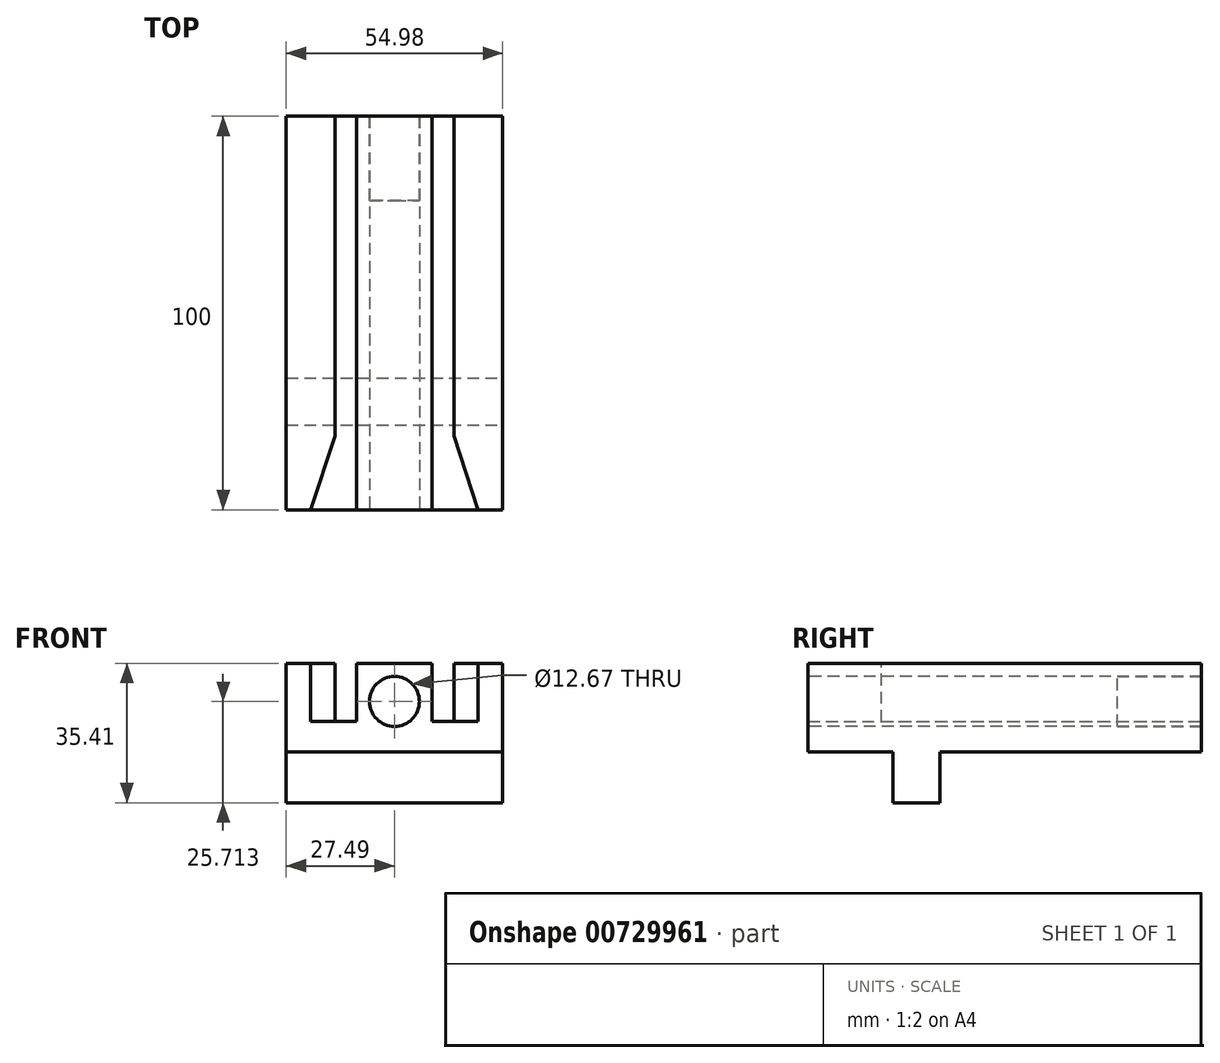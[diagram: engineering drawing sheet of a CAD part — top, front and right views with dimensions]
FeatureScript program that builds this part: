
annotation { "Feature Type Name" : "Feature", "Feature Type Description" : "" }
export const myFeature = defineFeature(function(context is Context, id is Id, definition is map)
    precondition{}
    {
        {
            var Q0;
            Q0=qCreatedBy(makeId("Front.planeOp"),FACE);
            var sketch = newSketch(context, id + "F0", { "sketchPlane" : qUnion([Q0])});
            skLineSegment(sketch, "E0.bottom", {"start": v(15.1, 10.3) * mm, "end": v(9.57, 10.3) * mm});
            skLineSegment(sketch, "E0.top", {"start": v(27.49, -10.3) * mm, "end": v(-27.49, -10.3) * mm});
            skLineSegment(sketch, "E0.left", {"start": v(27.49, 10.3) * mm, "end": v(27.49, -10.3) * mm});
            skLineSegment(sketch, "E0.right", {"start": v(-27.49, 10.3) * mm, "end": v(-27.49, -10.3) * mm});
            skPoint(sketch, "E0.middle", {"position": v(0, 0) * mm});
            skLineSegment(sketch, "E1.top", {"start": v(-9.57, 25.12) * mm, "end": v(9.57, 25.12) * mm});
            skLineSegment(sketch, "E1.left", {"start": v(-9.57, 10.3) * mm, "end": v(-9.57, 25.12) * mm});
            skLineSegment(sketch, "E1.right", {"start": v(9.57, 10.3) * mm, "end": v(9.57, 25.12) * mm});
            skPoint(sketch, "E1.middle", {"position": v(0, 10.3) * mm});
            skLineSegment(sketch, "E2.bottom", {"start": v(-27.49, -10.3) * mm, "end": v(-15.1, -10.3) * mm});
            skLineSegment(sketch, "E2.left", {"start": v(-27.49, -10.3) * mm, "end": v(-27.49, 25.12) * mm});
            skLineSegment(sketch, "E2.right", {"start": v(-15.1, 10.3) * mm, "end": v(-15.1, 25.12) * mm});
            skPoint(sketch, "E2.middle", {"position": v(-21.3, 25.12) * mm});
            skLineSegment(sketch, "E3", {"start": v(-15.1, 25.12) * mm, "end": v(-27.49, 25.12) * mm});
            skPoint(sketch, "E4.orphan", {"position": v(-15.1, 60.53) * mm});
            skPoint(sketch, "E5.orphan", {"position": v(-27.49, 60.53) * mm});
            skPoint(sketch, "E1.bottom.end.orphan", {"position": v(9.57, -4.53) * mm});
            skPoint(sketch, "E1.bottom.start.orphan", {"position": v(-9.57, -4.53) * mm});
            skLineSegment(sketch, "E6.trimOffspring", {"start": v(-9.57, 10.3) * mm, "end": v(-15.1, 10.3) * mm});
            skLineSegment(sketch, "E7.MirrorCS", {"start": v(15.1, 10.3) * mm, "end": v(15.1, 25.12) * mm});
            skLineSegment(sketch, "E8.MirrorCS", {"start": v(15.1, 25.12) * mm, "end": v(27.49, 25.12) * mm});
            skLineSegment(sketch, "E9.MirrorCS", {"start": v(27.49, -10.3) * mm, "end": v(27.49, 25.12) * mm});
            skSolve(sketch);
        }
        {
            var Q0;
            Q0 = qSketchRegion(id + "F0", true);
            extrude(context, id + "F1", {"entities" : qUnion([Q0]), "endBound" : BoundingType.SYMMETRIC, "depth" : 100 * mm, "offsetDistance" : 25 * mm});
        }
        {
            var Q0;
            Q0=makeQuery(id+"F1.opExtrude","SWEPT_FACE",FACE,{"disambiguationData":[OSD([sQuery(id+"F0.wireOp",EDGE,"E0.top"),sQuery(id+"F0.wireOp",EDGE,"E2.bottom")])]});
            var sketch = newSketch(context, id + "F2", { "sketchPlane" : qUnion([Q0])});
            skLineSegment(sketch, "E10.0.0", {"start": v(-27.49, -50) * mm, "end": v(27.49, -50) * mm, "construction": true});
            skLineSegment(sketch, "E10.0.1", {"start": v(27.49, -50) * mm, "end": v(27.49, 50) * mm, "construction": true});
            skLineSegment(sketch, "E10.0.2", {"start": v(27.49, 50) * mm, "end": v(-27.49, 50) * mm, "construction": true});
            skLineSegment(sketch, "E10.0.3", {"start": v(-27.49, 50) * mm, "end": v(-27.49, -50) * mm, "construction": true});
            skLineSegment(sketch, "E11.bottom", {"start": v(-27.49, 50) * mm, "end": v(27.49, 50) * mm});
            skLineSegment(sketch, "E11.top", {"start": v(-27.49, 28.41) * mm, "end": v(27.49, 28.41) * mm});
            skLineSegment(sketch, "E11.left", {"start": v(-27.49, 50) * mm, "end": v(-27.49, 28.41) * mm});
            skLineSegment(sketch, "E11.right", {"start": v(27.49, 50) * mm, "end": v(27.49, 28.41) * mm});
            skLineSegment(sketch, "E12.bottom", {"start": v(-27.49, 16.47) * mm, "end": v(27.49, 16.47) * mm});
            skLineSegment(sketch, "E12.top", {"start": v(-27.49, -50) * mm, "end": v(27.49, -50) * mm});
            skLineSegment(sketch, "E12.left", {"start": v(-27.49, 16.47) * mm, "end": v(-27.49, -50) * mm});
            skLineSegment(sketch, "E12.right", {"start": v(27.49, 16.47) * mm, "end": v(27.49, -50) * mm});
            skSolve(sketch);
        }
        {
            var Q0;
            Q0 = qSketchRegion(id + "F2", true);
            extrude(context, id + "F3", {"entities" : qUnion([Q0]), "operationType" : NewBodyOperationType.REMOVE, "oppositeDirection" : true, "depth" : 12.9 * mm, "offsetDistance" : 25 * mm});
        }
        {
            var Q0;
            Q0=makeQuery(id+"F1.opExtrude","SWEPT_FACE",FACE,{"disambiguationData":[OSD([sQuery(id+"F0.wireOp",EDGE,"E8.MirrorCS")])]});
            var sketch = newSketch(context, id + "F4", { "sketchPlane" : qUnion([Q0])});
            skLineSegment(sketch, "E13.0.0", {"start": v(-15.1, 50) * mm, "end": v(-27.49, 50) * mm, "construction": true});
            skLineSegment(sketch, "E13.0.1", {"start": v(-27.49, 50) * mm, "end": v(-27.49, -50) * mm, "construction": true});
            skLineSegment(sketch, "E13.0.2", {"start": v(-27.49, -50) * mm, "end": v(-21.3, -50) * mm, "construction": true});
            skLineSegment(sketch, "E13.0.3", {"start": v(-15.1, -31.3) * mm, "end": v(-15.1, 50) * mm, "construction": true});
            skLineSegment(sketch, "E14.0.0", {"start": v(27.49, 50) * mm, "end": v(15.1, 50) * mm, "construction": true});
            skLineSegment(sketch, "E14.0.1", {"start": v(15.1, 50) * mm, "end": v(15.1, -50) * mm, "construction": true});
            skLineSegment(sketch, "E14.0.2", {"start": v(15.1, -50) * mm, "end": v(27.49, -50) * mm, "construction": true});
            skLineSegment(sketch, "E14.0.3", {"start": v(27.49, -50) * mm, "end": v(27.49, 50) * mm, "construction": true});
            skLineSegment(sketch, "E15", {"start": v(0, -31.3) * mm, "end": v(27.49, -31.3) * mm, "construction": true});
            skLineSegment(sketch, "E16", {"start": v(-21.3, -50) * mm, "end": v(-15.1, -31.3) * mm});
            skLineSegment(sketch, "E17", {"start": v(0, 60.74) * mm, "end": v(0, -61.76) * mm, "construction": true});
            skPoint(sketch, "E18.orphan", {"position": v(-27.49, -31.3) * mm});
            skLineSegment(sketch, "E19", {"start": v(-15.1, -31.3) * mm, "end": v(-15.1, -50) * mm});
            skLineSegment(sketch, "E20", {"start": v(-21.3, -50) * mm, "end": v(-15.1, -50) * mm});
            skLineSegment(sketch, "E21.MirrorCS", {"start": v(21.3, -50) * mm, "end": v(15.1, -31.3) * mm});
            skLineSegment(sketch, "E22.MirrorCS", {"start": v(15.1, -31.3) * mm, "end": v(15.1, -50) * mm});
            skLineSegment(sketch, "E23.MirrorCS", {"start": v(21.3, -50) * mm, "end": v(15.1, -50) * mm});
            skSolve(sketch);
        }
        {
            var Q0;
            Q0 = qSketchRegion(id + "F4", true);
            var Q1;
            Q1=makeQuery(id+"F1.opExtrude","SWEPT_FACE",FACE,{"disambiguationData":[OSD([sQuery(id+"F0.wireOp",EDGE,"E6.trimOffspring")])]});
            extrude(context, id + "F5", {"entities" : qUnion([Q0]), "operationType" : NewBodyOperationType.REMOVE, "endBound" : BoundingType.UP_TO_SURFACE, "oppositeDirection" : true, "depth" : 25 * mm, "endBoundEntityFace" : qUnion([Q1]), "offsetDistance" : 25 * mm});
        }
        {
            var Q0;
            Q0=makeQuery(id+"F1.opExtrude","CAP_FACE",FACE,{"disambiguationData":[OSD([sQuery(id+"F0.wireOp",EDGE,"E0.bottom"),sQuery(id+"F0.wireOp",EDGE,"E0.top"),sQuery(id+"F0.wireOp",EDGE,"E1.top"),sQuery(id+"F0.wireOp",EDGE,"E1.left"),sQuery(id+"F0.wireOp",EDGE,"E1.right"),sQuery(id+"F0.wireOp",EDGE,"E2.bottom"),sQuery(id+"F0.wireOp",EDGE,"E2.left"),sQuery(id+"F0.wireOp",EDGE,"E2.right"),sQuery(id+"F0.wireOp",EDGE,"E3"),sQuery(id+"F0.wireOp",EDGE,"E6.trimOffspring"),sQuery(id+"F0.wireOp",EDGE,"E7.MirrorCS"),sQuery(id+"F0.wireOp",EDGE,"E8.MirrorCS"),sQuery(id+"F0.wireOp",EDGE,"E9.MirrorCS")])],"isStart":false});
            var sketch = newSketch(context, id + "F6", { "sketchPlane" : qUnion([Q0])});
            skCircle(sketch, "E24", {"center": v(0, 15.42) * mm, "radius": 6.33 * mm});
            skSolve(sketch);
        }
        {
            var Q0;
            Q0 = qSketchRegion(id + "F6", true);
            extrude(context, id + "F7", {"entities" : qUnion([Q0]), "operationType" : NewBodyOperationType.REMOVE, "oppositeDirection" : true, "depth" : 114.6 * mm, "offsetDistance" : 25 * mm});
        }
        {
            var Q0;
            Q0=makeQuery(id+"F1.opExtrude","CAP_FACE",FACE,{"disambiguationData":[OSD([sQuery(id+"F0.wireOp",EDGE,"E0.bottom"),sQuery(id+"F0.wireOp",EDGE,"E0.top"),sQuery(id+"F0.wireOp",EDGE,"E1.top"),sQuery(id+"F0.wireOp",EDGE,"E1.left"),sQuery(id+"F0.wireOp",EDGE,"E1.right"),sQuery(id+"F0.wireOp",EDGE,"E2.bottom"),sQuery(id+"F0.wireOp",EDGE,"E2.left"),sQuery(id+"F0.wireOp",EDGE,"E2.right"),sQuery(id+"F0.wireOp",EDGE,"E3"),sQuery(id+"F0.wireOp",EDGE,"E6.trimOffspring"),sQuery(id+"F0.wireOp",EDGE,"E7.MirrorCS"),sQuery(id+"F0.wireOp",EDGE,"E8.MirrorCS"),sQuery(id+"F0.wireOp",EDGE,"E9.MirrorCS")])],"isStart":true});
            var sketch = newSketch(context, id + "F8", { "sketchPlane" : qUnion([Q0])});
            skCircle(sketch, "E25.0", {"center": v(0, 15.42) * mm, "radius": 6.33 * mm});
            skSolve(sketch);
        }
        {
            var Q0;
            Q0 = qSketchRegion(id + "F8", true);
            extrude(context, id + "F9", {"entities" : qUnion([Q0]), "oppositeDirection" : true, "depth" : 21.4 * mm, "offsetDistance" : 25 * mm});
        }
    });
